# Revit family: QF_MARCO_MIX PB8
name_source: partatom
category: Specialty Equipment
revit_build: Autodesk Revit 2015 (Build: 20160512_0715(x64)
units: mm (PartAtom-declared; Revit-internal decimal feet)

## types (1)
- QF_MARCO_MIX PB8
    Apparent Power = 0 VA
    Cold Water Connection Height = 0 "
    Cold Water Flow = 0 GPM
    Cold Water Maximum Pressure = 0.00 psi
    Cold Water Minimum Pressure = 0.00 psi
    Cold Water RI Height = 0 "
    Cold Water Size = 1"
    Cold Water Temperature Recommended = 0 °F
    Conn Conduit = Yes
    Conn Plug = NEMA L6-20P
    Cycle = 60 Hz
    Depth = 13.862 "
    Description = MIX COUNTERTOP MULTI-TEMP WATER BOILERS/PUSH BUTTON
    Elec Conn Connection Height = 0 "
    Elec Conn RI Height = 0 "
    FL Amps = 12 A
    Foodservice Equipment Identifier = Yes
    Height = 23.307 "
    Identify Quantity as Lot = Yes
    Indirect Waste Connection Height = 0 "
    Indirect Waste Flow = 0 GPM
    Indirect Waste Size = 1"
    Length = 8.268 "
    Manufacturer = MARCO
    Max Overcurrent Protection = 0 A
    Min Ckt Ampacity = 0 A
    Model = MIX PB8
    Number of Poles = 1
    Phase = 1
    Volts = 230 V
    Waste Water Discharge Temperature = 0 °F
    Watts = 2800 W
    Weight in Pounds = 14

## geometry (parser evidence)
native form markers: Sweep x1
no freeform markers — native parametric forms only
